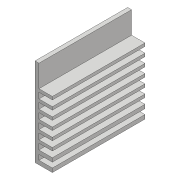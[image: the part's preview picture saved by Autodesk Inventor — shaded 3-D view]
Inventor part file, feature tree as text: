
AUTODESK INVENTOR PART (.ipt)
format: ipt  version: 2018 (Build 220112000, 112)  size: 176,128 bytes
history: native  units: mm
features: extrude x7, sketch x7, projected_geometry x5, mirror x1, pattern_linear x1
ambient origin geometry x8: Origin, YZ Plane, XZ Plane, XY Plane, X Axis, Y Axis, Z Axis, Center Point
bodies: Solid1 (feature_tree)
feature tree (21):
  extrude  "Extrusion1"  Depth=40.0mm
  extrude  "Extrusion2"  Depth=1.7mm
  mirror  "Mirror1"
  extrude  "Extrusion3"  Depth=2.2mm
  pattern_linear  "Rectangular Pattern1"  Count1=8 Spacing1=3.82mm
  extrude  "Extrusion4"  Depth=3.82mm TaperAngle=0.0deg
  extrude  "Extrusion5"  Depth=3.82mm TaperAngle=0.0deg
  extrude  "Extrusion8"  Depth=3.82mm TaperAngle=0.0deg
  extrude  "Extrusion9"  Depth=3.82mm TaperAngle=0.0deg
  sketch  "Sketch1"  dims[d0=20.0mm d1=40.0mm]
  sketch  "Sketch2"  dims[d2=40.0mm d3=0.0mm d4=1.7mm]
  projected_geometry  "Projected Loop1"
  sketch  "Sketch3"  dims[d5=4.2mm d6=2.2mm]
  projected_geometry  "Projected Loop2"
  sketch  "Sketch4"  dims[d7=85.0mm d8=0.0mm]
  projected_geometry  "Projected Loop3"
  sketch  "Sketch5"  dims[d9=1.3mm]
  sketch  "Sketch8"  dims[d10=2.52mm]
  projected_geometry  "Projected Loop5"
  sketch  "Sketch9"  dims[d11=85.0mm d12=0.0mm d13=80.0mm d15=3.82mm d16=2.5mm d17=0.0mm d18=10.0mm d19=0.0mm d32=10.0mm d33=0.0mm d34=2.0mm d35=0.0mm]
  projected_geometry  "Projected Loop6"
